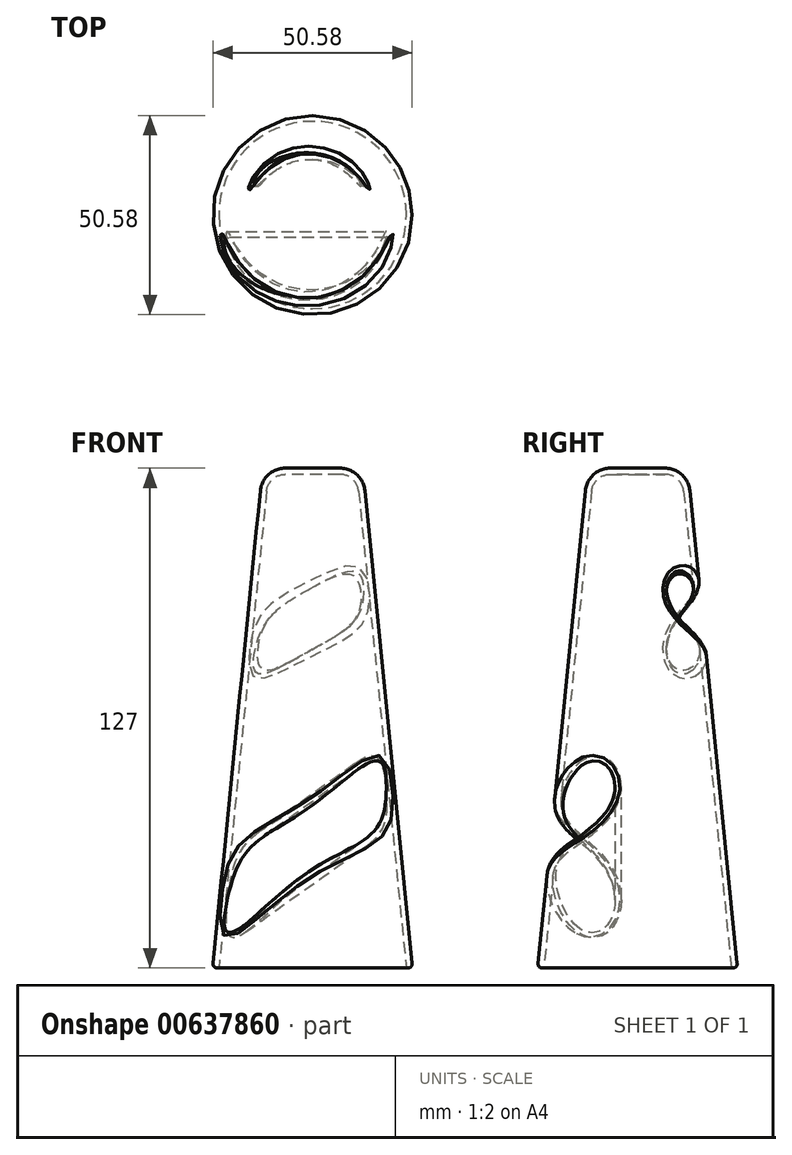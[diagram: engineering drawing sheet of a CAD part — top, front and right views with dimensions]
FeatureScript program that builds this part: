
annotation { "Feature Type Name" : "Feature", "Feature Type Description" : "" }
export const myFeature = defineFeature(function(context is Context, id is Id, definition is map)
    precondition{}
    {
        {
            var Q0;
            Q0=qCreatedBy(makeId("Top.planeOp"),FACE);
            var sketch = newSketch(context, id + "F0", { "sketchPlane" : qUnion([Q0])});
            skCircle(sketch, "E0", {"center": v(0, 0) * mm, "radius": 25.4 * mm});
            skSolve(sketch);
        }
        {
            var Q0;
            Q0=qCreatedBy(makeId("Top.planeOp"),FACE);
            cPlane(context, id + "F1", {"entities" : qUnion([Q0]), "cplaneType" : CPlaneType.OFFSET, "offset" : 127 * mm, "width" : 152.4 * mm, "height" : 152.4 * mm});
        }
        {
            var Q0;
            Q0=qCreatedBy(id+"F1.planeOp",FACE);
            var sketch = newSketch(context, id + "F2", { "sketchPlane" : qUnion([Q0])});
            skCircle(sketch, "E1", {"center": v(0, 0) * mm, "radius": 12.7 * mm});
            skSolve(sketch);
        }
        {
            var Q0;
            Q0=makeQuery(id+"F0.imprint","IMPRINT",FACE,{"disambiguationData":[TD([[makeQuery(id+"F0.imprint","IMPRINT",EDGE,{"derivedFrom":sQuery(id+"F0.wireOp",EDGE,"E0")}),1.0]])]});
            var Q1;
            Q1=makeQuery(id+"F2.imprint","IMPRINT",FACE,{"disambiguationData":[TD([[makeQuery(id+"F2.imprint","IMPRINT",EDGE,{"derivedFrom":sQuery(id+"F2.wireOp",EDGE,"E1")}),1.0]])]});
            loft(context, id + "F3", {"sheetProfilesArray" : [{ "sheetProfileEntities" : qUnion([Q0]) }, { "sheetProfileEntities" : qUnion([Q1]) }]});
        }
        {
            var Q0;
            Q0=qCreatedBy(makeId("Right.planeOp"),FACE);
            cPlane(context, id + "F4", {"entities" : qUnion([Q0]), "cplaneType" : CPlaneType.OFFSET, "offset" : 15.24 * mm, "width" : 152.4 * mm, "height" : 152.4 * mm});
        }
        {
            var Q0;
            Q0=qCreatedBy(makeId("Front.planeOp"),FACE);
            cPlane(context, id + "F5", {"entities" : qUnion([Q0]), "cplaneType" : CPlaneType.OFFSET, "offset" : 15.24 * mm, "width" : 152.4 * mm, "height" : 152.4 * mm});
        }
        {
            var Q0;
            Q0=qCreatedBy(id+"F5.planeOp",FACE);
            var sketch = newSketch(context, id + "F6", { "sketchPlane" : qUnion([Q0])});
            skLineSegment(sketch, "E2", {"start": v(-40.64, 3.7) * mm, "end": v(38.85, 60.26) * mm});
            skSolve(sketch);
        }
        {
            var Q0;
            Q0=sQuery(id+"F6.wireOp",VERTEX,"E2.end");
            var Q1;
            Q1=qCreatedBy(id+"F4.planeOp",FACE);
            cPlane(context, id + "F7", {"entities" : qUnion([Q0, Q1]), "cplaneType" : CPlaneType.PLANE_POINT, "offset" : 25.4 * mm, "width" : 152.4 * mm, "height" : 152.4 * mm});
        }
        {
            var Q0;
            Q0=qCreatedBy(id+"F7.planeOp",FACE);
            var sketch = newSketch(context, id + "F8", { "sketchPlane" : qUnion([Q0])});
            skCircle(sketch, "E3", {"center": v(-15.27, 60.38) * mm, "radius": 9.53 * mm});
            skSolve(sketch);
        }
        {
            var Q0;
            Q0=makeQuery(id+"F8.imprint","IMPRINT",FACE,{"disambiguationData":[TD([[makeQuery(id+"F8.imprint","IMPRINT",EDGE,{"derivedFrom":sQuery(id+"F8.wireOp",EDGE,"E3")}),1.0]])]});
            var Q1;
            Q1=sQuery(id+"F8.wireOp",EDGE,"E3");
            var Q2;
            Q2=sQuery(id+"F6.wireOp",EDGE,"E2");
            sweep(context, id + "F9", {"operationType" : NewBodyOperationType.REMOVE, "profiles" : qUnion([Q0]), "surfaceProfiles" : qUnion([Q1]), "path" : qUnion([Q2])});
        }
        {
            var Q0;
            Q0=makeQuery(id+"F9.boolean.opBoolean","INTERSECT",EDGE,{"derivedFrom":[makeQuery(id+"F3.opLoft","SWEPT_FACE",FACE,{"disambiguationData":[OSD([sQuery(id+"F0.wireOp",EDGE,"E0"),sQuery(id+"F2.wireOp",EDGE,"E1")])]}),makeQuery(id+"F9.opSweep","SWEPT_FACE",FACE,{"disambiguationData":[OSD([sQuery(id+"F6.wireOp",EDGE,"E2"),sQuery(id+"F8.wireOp",EDGE,"E3")])]})]});
            fillet(context, id + "F10", {"entities" : qUnion([Q0]), "radius" : 1.59 * mm, "tangentPropagation" : true, "allowEdgeOverflow" : false});
        }
        {
            var Q0;
            Q0=makeQuery(id+"F3.opLoft","MID_CAP_EDGE",EDGE,{"disambiguationData":[OSD([sQuery(id+"F0.wireOp",EDGE,"E0"),sQuery(id+"F2.wireOp",EDGE,"E1")])],"capPos":1.0});
            fillet(context, id + "F11", {"entities" : qUnion([Q0]), "radius" : 6.35 * mm, "tangentPropagation" : true, "allowEdgeOverflow" : false});
        }
        {
            var Q0;
            Q0=makeQuery(id+"F3.opLoft","MID_CAP_EDGE",EDGE,{"disambiguationData":[OSD([sQuery(id+"F0.wireOp",EDGE,"E0")])],"capPos":0.0});
            fillet(context, id + "F12", {"entities" : qUnion([Q0]), "radius" : 1.02 * mm, "tangentPropagation" : true, "allowEdgeOverflow" : false});
        }
        {
            var Q0;
            Q0=makeQuery(id+"F3.opLoft","CAP_FACE",FACE,{"disambiguationData":[OSD([makeQuery(id+"F0.imprint","IMPRINT",FACE,{"disambiguationData":[TD([[makeQuery(id+"F0.imprint","IMPRINT",EDGE,{"derivedFrom":sQuery(id+"F0.wireOp",EDGE,"E0")}),1.0]])]})])],"isStart":true});
            shell(context, id + "F13", {"entities" : qUnion([Q0]), "thickness" : 1.59 * mm});
        }
        {
            var Q0;
            Q0=qCreatedBy(makeId("Front.planeOp"),FACE);
            cPlane(context, id + "F14", {"entities" : qUnion([Q0]), "cplaneType" : CPlaneType.OFFSET, "offset" : 15.24 * mm, "oppositeDirection" : true, "width" : 152.4 * mm, "height" : 152.4 * mm});
        }
        {
            var Q0;
            Q0=qCreatedBy(id+"F14.planeOp",FACE);
            var sketch = newSketch(context, id + "F15", { "sketchPlane" : qUnion([Q0])});
            skLineSegment(sketch, "E4", {"start": v(42.75, 112.4) * mm, "end": v(-42.21, 65.44) * mm});
            skSolve(sketch);
        }
        {
            var Q0;
            Q0=sQuery(id+"F15.wireOp",VERTEX,"E4.start");
            var Q1;
            Q1=qCreatedBy(makeId("Right.planeOp"),FACE);
            cPlane(context, id + "F16", {"entities" : qUnion([Q0, Q1]), "cplaneType" : CPlaneType.PLANE_POINT, "offset" : 25.4 * mm, "width" : 152.4 * mm, "height" : 152.4 * mm});
        }
        {
            var Q0;
            Q0=qCreatedBy(id+"F16.planeOp",FACE);
            var sketch = newSketch(context, id + "F17", { "sketchPlane" : qUnion([Q0])});
            skCircle(sketch, "E5", {"center": v(15.29, 112.51) * mm, "radius": 7.94 * mm});
            skSolve(sketch);
        }
        {
            var Q0;
            Q0=makeQuery(id+"F17.imprint","IMPRINT",FACE,{"disambiguationData":[TD([[makeQuery(id+"F17.imprint","IMPRINT",EDGE,{"derivedFrom":sQuery(id+"F17.wireOp",EDGE,"E5")}),1.0]])]});
            var Q1;
            Q1=sQuery(id+"F15.wireOp",EDGE,"E4");
            sweep(context, id + "F18", {"operationType" : NewBodyOperationType.REMOVE, "profiles" : qUnion([Q0]), "path" : qUnion([Q1])});
        }
        {
            var Q0;
            Q0=makeQuery(id+"F18.boolean.opBoolean","INTERSECT",EDGE,{"derivedFrom":[makeQuery(id+"F3.opLoft","SWEPT_FACE",FACE,{"disambiguationData":[OSD([sQuery(id+"F0.wireOp",EDGE,"E0"),sQuery(id+"F2.wireOp",EDGE,"E1")])]}),makeQuery(id+"F18.opSweep","SWEPT_FACE",FACE,{"disambiguationData":[OSD([sQuery(id+"F15.wireOp",EDGE,"E4"),sQuery(id+"F17.wireOp",EDGE,"E5")])]})]});
            fillet(context, id + "F19", {"entities" : qUnion([Q0]), "radius" : 1.59 * mm, "tangentPropagation" : true, "allowEdgeOverflow" : false});
        }
    });
